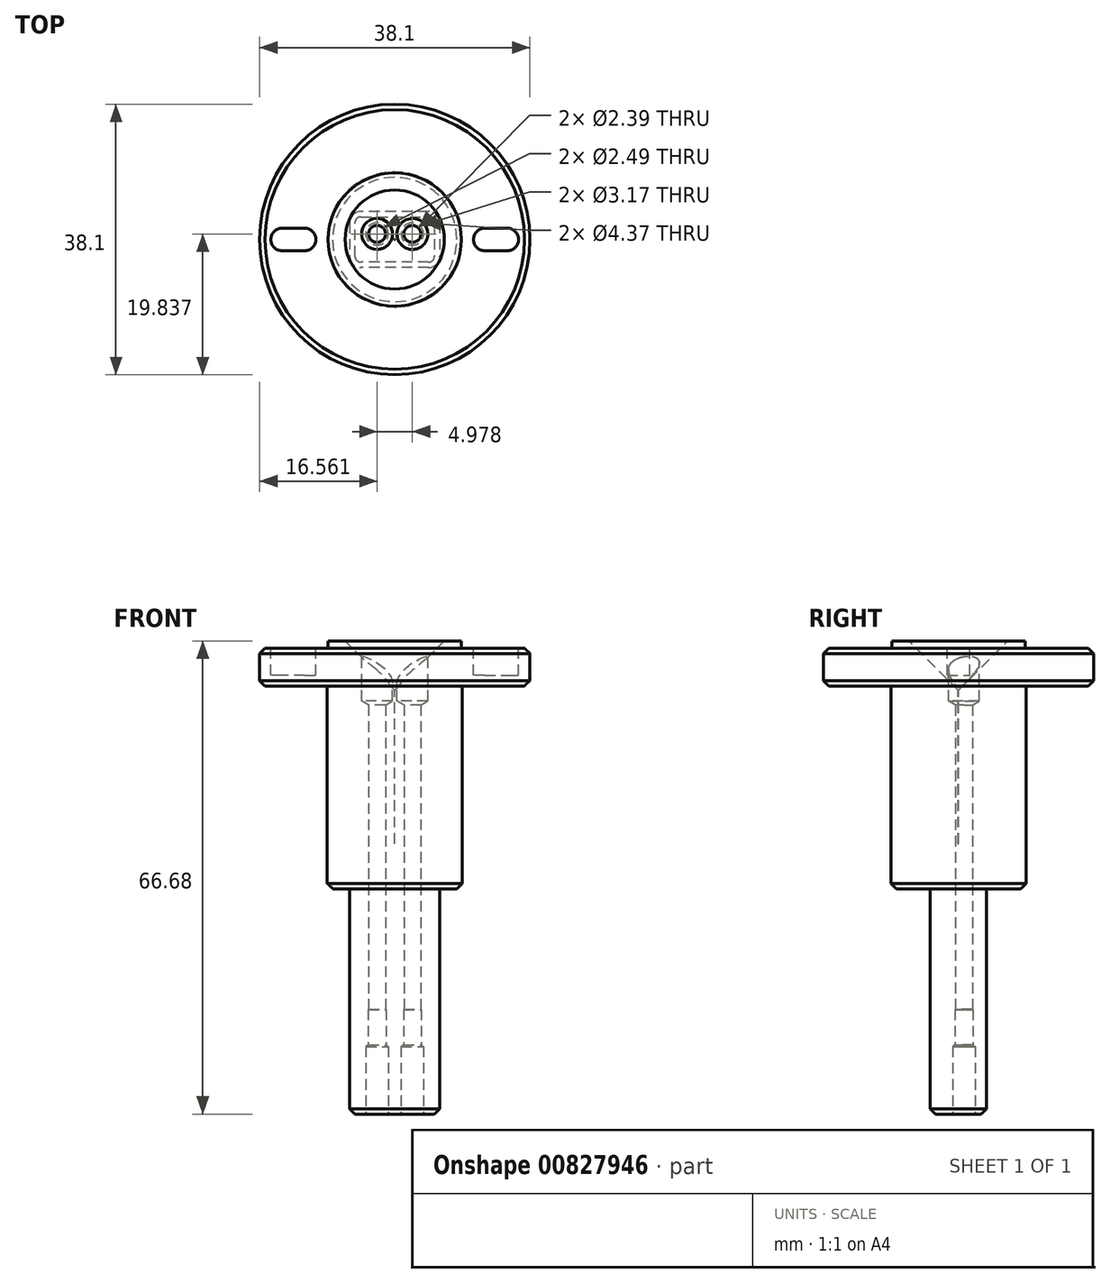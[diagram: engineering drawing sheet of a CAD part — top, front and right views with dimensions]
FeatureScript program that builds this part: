
annotation { "Feature Type Name" : "Feature", "Feature Type Description" : "" }
export const myFeature = defineFeature(function(context is Context, id is Id, definition is map)
    precondition{}
    {
        {
            var Q0;
            Q0=qCreatedBy(makeId("Top.planeOp"),FACE);
            var sketch = newSketch(context, id + "F0", { "sketchPlane" : qUnion([Q0])});
            skCircle(sketch, "E0", {"center": v(0, 0) * mm, "radius": 19.05 * mm});
            skSolve(sketch);
        }
        {
            var Q0;
            Q0=makeQuery(id+"F0.imprint","IMPRINT",FACE,{"disambiguationData":[TD([[makeQuery(id+"F0.imprint","IMPRINT",EDGE,{"derivedFrom":sQuery(id+"F0.wireOp",EDGE,"E0")}),1.0]])]});
            extrude(context, id + "F1", {"entities" : qUnion([Q0]), "depth" : 5.33 * mm, "offsetDistance" : 25.4 * mm});
        }
        {
            var Q0;
            Q0=makeQuery(id+"F1.opExtrude","CAP_FACE",FACE,{"disambiguationData":[OSD([sQuery(id+"F0.wireOp",EDGE,"E0")])],"isStart":false});
            var sketch = newSketch(context, id + "F2", { "sketchPlane" : qUnion([Q0])});
            skCircle(sketch, "E1", {"center": v(0, 0) * mm, "radius": 9.4 * mm});
            skSolve(sketch);
        }
        {
            var Q0;
            Q0=makeQuery(id+"F2.imprint","IMPRINT",FACE,{"disambiguationData":[TD([[makeQuery(id+"F2.imprint","IMPRINT",EDGE,{"derivedFrom":sQuery(id+"F2.wireOp",EDGE,"E1")}),1.0]])]});
            extrude(context, id + "F3", {"entities" : qUnion([Q0]), "operationType" : NewBodyOperationType.ADD, "depth" : 1.02 * mm, "offsetDistance" : 25.4 * mm});
        }
        {
            var Q0;
            Q0=makeQuery(id+"F1.opExtrude","CAP_FACE",FACE,{"disambiguationData":[OSD([sQuery(id+"F0.wireOp",EDGE,"E0")])],"isStart":true});
            var sketch = newSketch(context, id + "F4", { "sketchPlane" : qUnion([Q0])});
            skCircle(sketch, "E2", {"center": v(0, 0) * mm, "radius": 9.53 * mm});
            skSolve(sketch);
        }
        {
            var Q0;
            Q0=makeQuery(id+"F4.imprint","IMPRINT",FACE,{"disambiguationData":[TD([[makeQuery(id+"F4.imprint","IMPRINT",EDGE,{"derivedFrom":sQuery(id+"F4.wireOp",EDGE,"E2")}),1.0]])]});
            extrude(context, id + "F5", {"entities" : qUnion([Q0]), "operationType" : NewBodyOperationType.ADD, "depth" : 28.57 * mm, "offsetDistance" : 25.4 * mm});
        }
        {
            var Q0;
            Q0=makeQuery(id+"F5.opExtrude","CAP_FACE",FACE,{"disambiguationData":[OSD([sQuery(id+"F4.wireOp",EDGE,"E2")])],"isStart":false});
            var sketch = newSketch(context, id + "F6", { "sketchPlane" : qUnion([Q0])});
            skLineSegment(sketch, "E3.bottom", {"start": v(6.35, -3.96) * mm, "end": v(-6.35, -3.96) * mm});
            skLineSegment(sketch, "E3.top", {"start": v(6.35, 3.96) * mm, "end": v(-6.35, 3.96) * mm});
            skLineSegment(sketch, "E3.left", {"start": v(6.35, -3.96) * mm, "end": v(6.35, 3.96) * mm});
            skLineSegment(sketch, "E3.right", {"start": v(-6.35, -3.96) * mm, "end": v(-6.35, 3.96) * mm});
            skPoint(sketch, "E3.middle", {"position": v(0, 0) * mm});
            skSolve(sketch);
        }
        {
            var Q0;
            Q0=makeQuery(id+"F6.imprint","IMPRINT",FACE,{"disambiguationData":[TD([[makeQuery(id+"F6.imprint","IMPRINT",EDGE,{"derivedFrom":sQuery(id+"F6.wireOp",EDGE,"E3.bottom")}),-1.0]])]});
            extrude(context, id + "F7", {"entities" : qUnion([Q0]), "operationType" : NewBodyOperationType.ADD, "depth" : 31.75 * mm, "offsetDistance" : 25.4 * mm});
        }
        {
            var Q0;
            Q0=makeQuery(id+"F3.opExtrude","CAP_FACE",FACE,{"disambiguationData":[OSD([sQuery(id+"F2.wireOp",EDGE,"E1")])],"isStart":false});
            var sketch = newSketch(context, id + "F8", { "sketchPlane" : qUnion([Q0])});
            skPoint(sketch, "E4", {"position": v(0, 0) * mm});
            skSolve(sketch);
        }
        {
            var Q0;
            Q0=sQuery(id+"F8.wireOp",VERTEX,"E4");
            var Q1;
            Q1=makeQuery(id+"F1.opExtrude","SWEPT_BODY",BODY,{"disambiguationData":[OSD([sQuery(id+"F0.wireOp",EDGE,"E0")])]});
            hole(context, id + "F9", {"style" : HoleStyle.C_SINK, "endStyle" : HoleEndStyle.BLIND, "standardTappedOrClearance" : lookupTablePath({ "standard" : "ANSI", "size" : "1/2 (0.5)", "type" : "Drilled" }), "standardBlindInLast" : lookupTablePath({ "standard" : "ANSI", "size" : "1/2", "type" : "Drilled" }), "holeDiameter" : 1 / 50.8 * mm, "cSinkDiameter" : 13.97 * mm, "cSinkAngle" : 90 * degree, "majorDiameter" : 6.35 * mm, "holeDepth" : 28.57 * mm, "isTappedThrough" : true, "tappedDepth" : 12.7 * mm, "tapClearance" : 3, "locations" : qUnion([Q0]), "scope" : qUnion([Q1])});
        }
        {
            var Q0;
            Q0=makeQuery(id+"F5.opExtrude","CAP_EDGE",EDGE,{"disambiguationData":[OSD([sQuery(id+"F4.wireOp",EDGE,"E2")])],"isStart":false});
            var Q1;
            Q1=makeQuery(id+"F1.opExtrude","CAP_EDGE",EDGE,{"disambiguationData":[OSD([sQuery(id+"F0.wireOp",EDGE,"E0")])],"isStart":true});
            var Q2;
            Q2=makeQuery(id+"F1.opExtrude","CAP_EDGE",EDGE,{"disambiguationData":[OSD([sQuery(id+"F0.wireOp",EDGE,"E0")])],"isStart":false});
            chamfer(context, id + "F10", {"entities" : qUnion([Q0, Q1, Q2]), "width" : 0.76 * mm, "tangentPropagation" : true});
        }
        {
            var Q0;
            Q0=makeQuery(id+"F7.opExtrude","CAP_FACE",FACE,{"disambiguationData":[OSD([sQuery(id+"F6.wireOp",EDGE,"E3.bottom"),sQuery(id+"F6.wireOp",EDGE,"E3.top"),sQuery(id+"F6.wireOp",EDGE,"E3.left"),sQuery(id+"F6.wireOp",EDGE,"E3.right")])],"isStart":false});
            var sketch = newSketch(context, id + "F11", { "sketchPlane" : qUnion([Q0])});
            skPoint(sketch, "E5", {"position": v(2.49, -0.79) * mm});
            skPoint(sketch, "E6", {"position": v(-2.49, -0.79) * mm});
            skSolve(sketch);
        }
        {
            var Q0;
            Q0=sQuery(id+"F11.wireOp",VERTEX,"E5");
            var Q1;
            Q1=sQuery(id+"F11.wireOp",VERTEX,"E6");
            var Q2;
            Q2=makeQuery(id+"F1.opExtrude","SWEPT_BODY",BODY,{"disambiguationData":[OSD([sQuery(id+"F0.wireOp",EDGE,"E0")])]});
            hole(context, id + "F12", {"style" : HoleStyle.SIMPLE, "endStyle" : HoleEndStyle.THROUGH, "holeDiameter" : 2.4 * mm, "majorDiameter" : 6.35 * mm, "isTappedThrough" : true, "tappedDepth" : 12.7 * mm, "tapClearance" : 3, "locations" : qUnion([Q0, Q1]), "scope" : qUnion([Q2])});
        }
        {
            var Q0;
            Q0=makeQuery(id+"F7.opExtrude","CAP_FACE",FACE,{"disambiguationData":[OSD([sQuery(id+"F6.wireOp",EDGE,"E3.bottom"),sQuery(id+"F6.wireOp",EDGE,"E3.top"),sQuery(id+"F6.wireOp",EDGE,"E3.left"),sQuery(id+"F6.wireOp",EDGE,"E3.right")])],"isStart":false});
            var sketch = newSketch(context, id + "F13", { "sketchPlane" : qUnion([Q0])});
            skPoint(sketch, "E7", {"position": v(2.49, -0.79) * mm});
            skPoint(sketch, "E8", {"position": v(-2.49, -0.79) * mm});
            skSolve(sketch);
        }
        {
            var Q0;
            Q0=sQuery(id+"F13.wireOp",VERTEX,"E7");
            var Q1;
            Q1=sQuery(id+"F13.wireOp",VERTEX,"E8");
            var Q2;
            Q2=makeQuery(id+"F1.opExtrude","SWEPT_BODY",BODY,{"disambiguationData":[OSD([sQuery(id+"F0.wireOp",EDGE,"E0")])]});
            hole(context, id + "F14", {"style" : HoleStyle.SIMPLE, "endStyle" : HoleEndStyle.BLIND, "holeDiameter" : 2.5 * mm, "majorDiameter" : 6.35 * mm, "holeDepth" : 14.73 * mm, "isTappedThrough" : true, "tappedDepth" : 12.7 * mm, "tapClearance" : 3, "locations" : qUnion([Q0, Q1]), "scope" : qUnion([Q2])});
        }
        {
            var Q0;
            Q0=makeQuery(id+"F7.opExtrude","CAP_FACE",FACE,{"disambiguationData":[OSD([sQuery(id+"F6.wireOp",EDGE,"E3.bottom"),sQuery(id+"F6.wireOp",EDGE,"E3.top"),sQuery(id+"F6.wireOp",EDGE,"E3.left"),sQuery(id+"F6.wireOp",EDGE,"E3.right")])],"isStart":false});
            var sketch = newSketch(context, id + "F15", { "sketchPlane" : qUnion([Q0])});
            skPoint(sketch, "E9", {"position": v(2.49, -0.79) * mm});
            skPoint(sketch, "E10", {"position": v(-2.49, -0.79) * mm});
            skSolve(sketch);
        }
        {
            var Q0;
            Q0=sQuery(id+"F15.wireOp",VERTEX,"E9");
            var Q1;
            Q1=sQuery(id+"F15.wireOp",VERTEX,"E10");
            var Q2;
            Q2=makeQuery(id+"F1.opExtrude","SWEPT_BODY",BODY,{"disambiguationData":[OSD([sQuery(id+"F0.wireOp",EDGE,"E0")])]});
            hole(context, id + "F16", {"style" : HoleStyle.SIMPLE, "endStyle" : HoleEndStyle.BLIND, "holeDiameter" : 3.17 * mm, "majorDiameter" : 6.35 * mm, "holeDepth" : 9.52 * mm, "isTappedThrough" : true, "tappedDepth" : 12.7 * mm, "tapClearance" : 3, "locations" : qUnion([Q0, Q1]), "scope" : qUnion([Q2])});
        }
        {
            var Q0;
            Q0=makeQuery(id+"F3.opExtrude","CAP_FACE",FACE,{"disambiguationData":[OSD([sQuery(id+"F2.wireOp",EDGE,"E1")])],"isStart":false});
            var sketch = newSketch(context, id + "F17", { "sketchPlane" : qUnion([Q0])});
            skPoint(sketch, "E11", {"position": v(2.49, 0.79) * mm});
            skPoint(sketch, "E12", {"position": v(-2.49, 0.79) * mm});
            skSolve(sketch);
        }
        {
            var Q0;
            Q0=sQuery(id+"F17.wireOp",VERTEX,"E11");
            var Q1;
            Q1=sQuery(id+"F17.wireOp",VERTEX,"E12");
            var Q2;
            Q2=makeQuery(id+"F1.opExtrude","SWEPT_BODY",BODY,{"disambiguationData":[OSD([sQuery(id+"F0.wireOp",EDGE,"E0")])]});
            hole(context, id + "F18", {"style" : HoleStyle.SIMPLE, "endStyle" : HoleEndStyle.BLIND, "holeDiameter" : 4.37 * mm, "majorDiameter" : 6.35 * mm, "holeDepth" : 1.9 * mm, "isTappedThrough" : true, "tappedDepth" : 12.7 * mm, "tapClearance" : 3, "locations" : qUnion([Q0, Q1]), "scope" : qUnion([Q2])});
        }
        {
            var Q0;
            Q0=makeQuery(id+"F1.opExtrude","CAP_FACE",FACE,{"disambiguationData":[OSD([sQuery(id+"F0.wireOp",EDGE,"E0")])],"isStart":false});
            var sketch = newSketch(context, id + "F19", { "sketchPlane" : qUnion([Q0])});
            skPoint(sketch, "E13", {"position": v(12.7, 0) * mm});
            skPoint(sketch, "E14", {"position": v(-12.7, 0) * mm});
            skPoint(sketch, "E15", {"position": v(-15.88, 0) * mm});
            skPoint(sketch, "E16", {"position": v(15.88, 0) * mm});
            skCircle(sketch, "E17", {"center": v(12.7, 0) * mm, "radius": 1.59 * mm});
            skCircle(sketch, "E18", {"center": v(15.88, 0) * mm, "radius": 1.59 * mm});
            skCircle(sketch, "E19", {"center": v(-12.7, 0) * mm, "radius": 1.59 * mm});
            skCircle(sketch, "E20", {"center": v(-15.88, 0) * mm, "radius": 1.59 * mm});
            skLineSegment(sketch, "E21", {"start": v(15.88, -1.59) * mm, "end": v(12.7, -1.59) * mm});
            skLineSegment(sketch, "E22", {"start": v(12.7, -1.59) * mm, "end": v(12.7, 1.59) * mm});
            skLineSegment(sketch, "E23", {"start": v(12.7, 1.59) * mm, "end": v(15.88, 1.59) * mm});
            skLineSegment(sketch, "E24", {"start": v(-12.7, -1.59) * mm, "end": v(-15.88, -1.59) * mm});
            skLineSegment(sketch, "E25", {"start": v(-12.7, 1.59) * mm, "end": v(-15.88, 1.59) * mm});
            skSolve(sketch);
        }
        {
            var Q0;
            {var subQ0=sQuery(id+"F19.wireOp",EDGE,"E18");var subQ1=makeQuery(id+"F19.imprint","INTERSECT",VERTEX,{"derivedFrom":[subQ0,sQuery(id+"F19.wireOp",EDGE,"E23")]});Q0=makeQuery(id+"F19.imprint","IMPRINT",FACE,{"disambiguationData":[TD([[makeQuery(id+"F19.imprint","IMPRINT",EDGE,{"disambiguationData":[TD([[subQ1,-1.0]])],"derivedFrom":subQ0}),1.0]])]});}
            var Q1;
            {var subQ0=sQuery(id+"F19.wireOp",EDGE,"E22");Q1=makeQuery(id+"F19.imprint","IMPRINT",FACE,{"disambiguationData":[TD([[makeQuery(id+"F19.imprint","IMPRINT",EDGE,{"derivedFrom":subQ0}),-1.0]])]});}
            var Q2;
            {var subQ0=sQuery(id+"F19.wireOp",EDGE,"E23");Q2=makeQuery(id+"F19.imprint","IMPRINT",FACE,{"disambiguationData":[TD([[makeQuery(id+"F19.imprint","IMPRINT",EDGE,{"derivedFrom":subQ0}),-1.0]])]});}
            var Q3;
            {var subQ0=sQuery(id+"F19.wireOp",EDGE,"E22");Q3=makeQuery(id+"F19.imprint","IMPRINT",FACE,{"disambiguationData":[TD([[makeQuery(id+"F19.imprint","IMPRINT",EDGE,{"derivedFrom":subQ0}),1.0]])]});}
            var Q4;
            {var subQ0=sQuery(id+"F19.wireOp",EDGE,"E21");Q4=makeQuery(id+"F19.imprint","IMPRINT",FACE,{"disambiguationData":[TD([[makeQuery(id+"F19.imprint","IMPRINT",EDGE,{"derivedFrom":subQ0}),-1.0]])]});}
            var Q5;
            {var subQ0=sQuery(id+"F19.wireOp",EDGE,"E19");var subQ1=makeQuery(id+"F19.imprint","INTERSECT",VERTEX,{"derivedFrom":[subQ0,sQuery(id+"F19.wireOp",EDGE,"E25")]});Q5=makeQuery(id+"F19.imprint","IMPRINT",FACE,{"disambiguationData":[TD([[makeQuery(id+"F19.imprint","IMPRINT",EDGE,{"disambiguationData":[TD([[subQ1,-1.0]])],"derivedFrom":subQ0}),1.0]])]});}
            var Q6;
            {var subQ0=sQuery(id+"F19.wireOp",EDGE,"E24");Q6=makeQuery(id+"F19.imprint","IMPRINT",FACE,{"disambiguationData":[TD([[makeQuery(id+"F19.imprint","IMPRINT",EDGE,{"derivedFrom":subQ0}),-1.0]])]});}
            var Q7;
            {var subQ0=sQuery(id+"F19.wireOp",EDGE,"E25");Q7=makeQuery(id+"F19.imprint","IMPRINT",FACE,{"disambiguationData":[TD([[makeQuery(id+"F19.imprint","IMPRINT",EDGE,{"derivedFrom":subQ0}),1.0]])]});}
            var Q8;
            {var subQ0=sQuery(id+"F19.wireOp",EDGE,"E20");var subQ1=makeQuery(id+"F19.imprint","INTERSECT",VERTEX,{"derivedFrom":[subQ0,sQuery(id+"F19.wireOp",EDGE,"E25")]});Q8=makeQuery(id+"F19.imprint","IMPRINT",FACE,{"disambiguationData":[TD([[makeQuery(id+"F19.imprint","IMPRINT",EDGE,{"disambiguationData":[TD([[subQ1,1.0]])],"derivedFrom":subQ0}),1.0]])]});}
            extrude(context, id + "F20", {"entities" : qUnion([Q0, Q1, Q2, Q3, Q4, Q5, Q6, Q7, Q8]), "operationType" : NewBodyOperationType.REMOVE, "oppositeDirection" : true, "depth" : 3.8 * mm, "offsetDistance" : 25.4 * mm});
        }
        {
            var Q0;
            Q0=makeQuery(id+"F7.opExtrude","SWEPT_EDGE",EDGE,{"disambiguationData":[OSD([sQuery(id+"F6.wireOp",EDGE,"E3.bottom"),sQuery(id+"F6.wireOp",EDGE,"E3.left")])]});
            var Q1;
            Q1=makeQuery(id+"F7.opExtrude","SWEPT_EDGE",EDGE,{"disambiguationData":[OSD([sQuery(id+"F6.wireOp",EDGE,"E3.top"),sQuery(id+"F6.wireOp",EDGE,"E3.left")])]});
            var Q2;
            Q2=makeQuery(id+"F7.opExtrude","SWEPT_EDGE",EDGE,{"disambiguationData":[OSD([sQuery(id+"F6.wireOp",EDGE,"E3.top"),sQuery(id+"F6.wireOp",EDGE,"E3.right")])]});
            var Q3;
            Q3=makeQuery(id+"F7.opExtrude","SWEPT_EDGE",EDGE,{"disambiguationData":[OSD([sQuery(id+"F6.wireOp",EDGE,"E3.bottom"),sQuery(id+"F6.wireOp",EDGE,"E3.right")])]});
            fillet(context, id + "F21", {"entities" : qUnion([Q0, Q1, Q2, Q3]), "radius" : 1.57 * mm, "tangentPropagation" : true, "allowEdgeOverflow" : false});
        }
        {
            var Q0;
            Q0=makeQuery(id+"F7.opExtrude","CAP_EDGE",EDGE,{"disambiguationData":[OSD([sQuery(id+"F6.wireOp",EDGE,"E3.left")])],"isStart":false});
            var Q1;
            {var subQ0=sQuery(id+"F6.wireOp",EDGE,"E3.left");var subQ1=sQuery(id+"F6.wireOp",EDGE,"E3.top");Q1=makeQuery(id+"F21.opFillet","BLEND_EDGE",EDGE,{"blendedFrom":[makeQuery(id+"F7.opExtrude","SWEPT_EDGE",EDGE,{"disambiguationData":[OSD([subQ1,subQ0])]}),makeQuery(id+"F7.opExtrude","CAP_FACE",FACE,{"disambiguationData":[OSD([sQuery(id+"F6.wireOp",EDGE,"E3.bottom"),subQ1,subQ0,sQuery(id+"F6.wireOp",EDGE,"E3.right")])],"isStart":false})],"blendedInto":[makeQuery(id+"F7.opExtrude","CAP_FACE",FACE,{"disambiguationData":[OSD([sQuery(id+"F6.wireOp",EDGE,"E3.bottom"),subQ1,subQ0,sQuery(id+"F6.wireOp",EDGE,"E3.right")])],"isStart":false})]});}
            var Q2;
            Q2=makeQuery(id+"F7.opExtrude","CAP_EDGE",EDGE,{"disambiguationData":[OSD([sQuery(id+"F6.wireOp",EDGE,"E3.top")])],"isStart":false});
            var Q3;
            Q3=makeQuery(id+"F7.opExtrude","CAP_EDGE",EDGE,{"disambiguationData":[OSD([sQuery(id+"F6.wireOp",EDGE,"E3.right")])],"isStart":false});
            var Q4;
            {var subQ0=sQuery(id+"F6.wireOp",EDGE,"E3.right");var subQ1=sQuery(id+"F6.wireOp",EDGE,"E3.top");Q4=makeQuery(id+"F21.opFillet","BLEND_EDGE",EDGE,{"blendedFrom":[makeQuery(id+"F7.opExtrude","SWEPT_EDGE",EDGE,{"disambiguationData":[OSD([subQ1,subQ0])]}),makeQuery(id+"F7.opExtrude","CAP_FACE",FACE,{"disambiguationData":[OSD([sQuery(id+"F6.wireOp",EDGE,"E3.bottom"),subQ1,sQuery(id+"F6.wireOp",EDGE,"E3.left"),subQ0])],"isStart":false})],"blendedInto":[makeQuery(id+"F7.opExtrude","CAP_FACE",FACE,{"disambiguationData":[OSD([sQuery(id+"F6.wireOp",EDGE,"E3.bottom"),subQ1,sQuery(id+"F6.wireOp",EDGE,"E3.left"),subQ0])],"isStart":false})]});}
            var Q5;
            Q5=makeQuery(id+"F7.opExtrude","CAP_EDGE",EDGE,{"disambiguationData":[OSD([sQuery(id+"F6.wireOp",EDGE,"E3.bottom")])],"isStart":false});
            var Q6;
            {var subQ0=sQuery(id+"F6.wireOp",EDGE,"E3.left");var subQ1=sQuery(id+"F6.wireOp",EDGE,"E3.bottom");Q6=makeQuery(id+"F21.opFillet","BLEND_EDGE",EDGE,{"blendedFrom":[makeQuery(id+"F7.opExtrude","SWEPT_EDGE",EDGE,{"disambiguationData":[OSD([subQ1,subQ0])]}),makeQuery(id+"F7.opExtrude","CAP_FACE",FACE,{"disambiguationData":[OSD([subQ1,sQuery(id+"F6.wireOp",EDGE,"E3.top"),subQ0,sQuery(id+"F6.wireOp",EDGE,"E3.right")])],"isStart":false})],"blendedInto":[makeQuery(id+"F7.opExtrude","CAP_FACE",FACE,{"disambiguationData":[OSD([subQ1,sQuery(id+"F6.wireOp",EDGE,"E3.top"),subQ0,sQuery(id+"F6.wireOp",EDGE,"E3.right")])],"isStart":false})]});}
            chamfer(context, id + "F22", {"entities" : qUnion([Q0, Q1, Q2, Q3, Q4, Q5, Q6]), "width" : 0.76 * mm, "tangentPropagation" : true});
        }
    });
